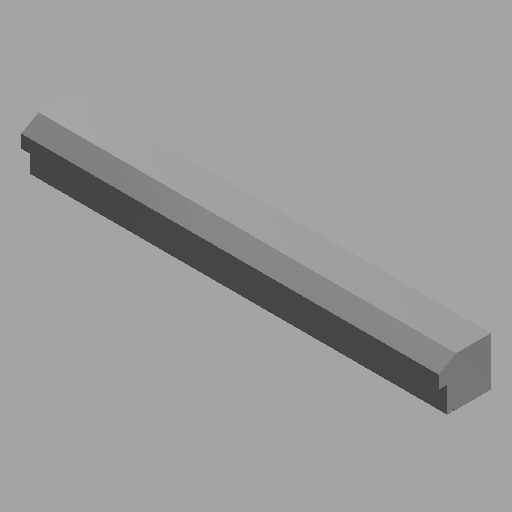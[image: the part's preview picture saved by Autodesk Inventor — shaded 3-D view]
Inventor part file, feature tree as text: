
AUTODESK INVENTOR PART (.ipt)
format: ipt  version: 2023 (Build 270158030, 158C)  size: 104,448 bytes
history: native  units: mm (DEFAULTED — no unit token found)
features: extrude x2, sketch x2
ambient origin geometry x8: Origin, YZ Plane, XZ Plane, XY Plane, X Axis, Y Axis, Z Axis, Center Point
bodies: Solid1 (feature_tree)
feature tree (4):
  extrude  "Extrusion1"  Depth=25.4mm TaperAngle=0.0deg
  extrude  "Extrusion2"  [1 undecoded]
  sketch  "Sketch1"  dims[d0=25.4mm d1=0.0mm d2=25.4mm d3=0.0mm]
  sketch  "Sketch2"
note: 1 required parameter value undecoded (feature->parameter linkage not recoverable at this tier; creation-order binding heuristic only, values carry confidence <= 0.55)
